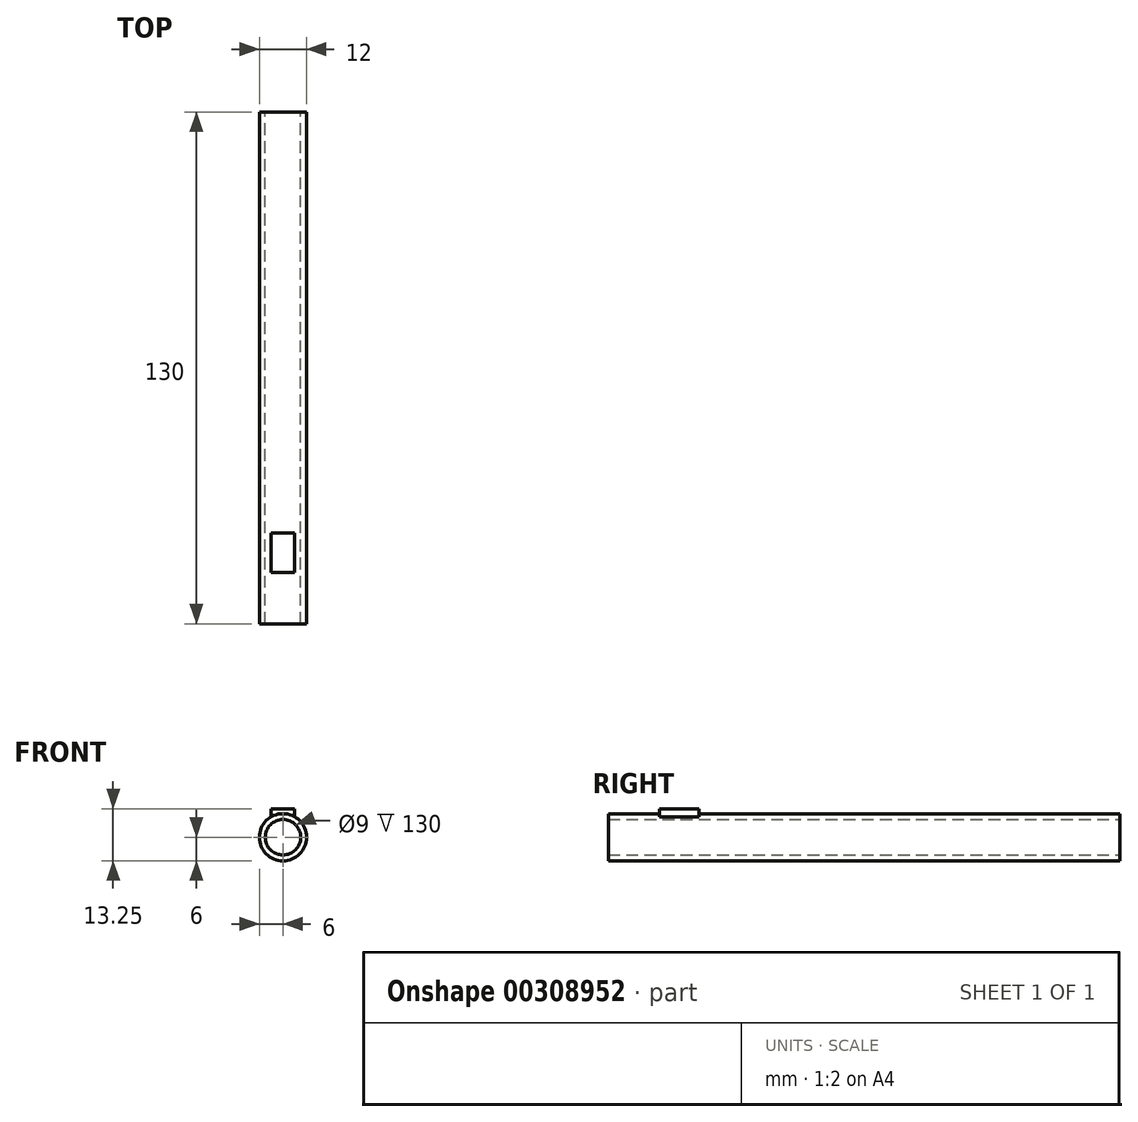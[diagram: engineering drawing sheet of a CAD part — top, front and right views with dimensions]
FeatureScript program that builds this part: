
annotation { "Feature Type Name" : "Feature", "Feature Type Description" : "" }
export const myFeature = defineFeature(function(context is Context, id is Id, definition is map)
    precondition{}
    {
        {
            var Q0;
            Q0=qCreatedBy(makeId("Front.planeOp"),FACE);
            var sketch = newSketch(context, id + "F0", { "sketchPlane" : qUnion([Q0])});
            skCircle(sketch, "E0", {"center": v(0, 0) * mm, "radius": 4.5 * mm});
            skCircle(sketch, "E1", {"center": v(0, 0) * mm, "radius": 6 * mm});
            skSolve(sketch);
        }
        {
            var Q0;
            Q0=makeQuery(id+"F0.imprint","IMPRINT",FACE,{"disambiguationData":[TD([[makeQuery(id+"F0.imprint","IMPRINT",EDGE,{"derivedFrom":sQuery(id+"F0.wireOp",EDGE,"E0")}),-1.0]])]});
            extrude(context, id + "F1", {"entities" : qUnion([Q0]), "depth" : 130 * mm, "offsetDistance" : 25 * mm});
        }
        {
            var Q0;
            Q0=makeQuery(id+"F1.opExtrude","CAP_FACE",FACE,{"disambiguationData":[OSD([sQuery(id+"F0.wireOp",EDGE,"E0"),sQuery(id+"F0.wireOp",EDGE,"E1")])],"isStart":false});
            var sketch = newSketch(context, id + "F2", { "sketchPlane" : qUnion([Q0])});
            skLineSegment(sketch, "E2.bottom", {"start": v(10, 7.25) * mm, "end": v(-10, 7.25) * mm});
            skLineSegment(sketch, "E2.top", {"start": v(10, -7.25) * mm, "end": v(-10, -7.25) * mm});
            skLineSegment(sketch, "E2.left", {"start": v(10, 7.25) * mm, "end": v(10, -7.25) * mm});
            skLineSegment(sketch, "E2.right", {"start": v(-10, 7.25) * mm, "end": v(-10, -7.25) * mm});
            skPoint(sketch, "E2.middle", {"position": v(0, 0) * mm});
            skLineSegment(sketch, "E3", {"start": v(0, 7.25) * mm, "end": v(0, 6) * mm});
            skLineSegment(sketch, "E4", {"start": v(3, 7.25) * mm, "end": v(3, 5.2) * mm});
            skLineSegment(sketch, "E5", {"start": v(-3, 7.25) * mm, "end": v(-3, 5.2) * mm});
            skSolve(sketch);
        }
        {
            var Q0;
            {var subQ0=sQuery(id+"F2.wireOp",EDGE,"E3");Q0=makeQuery(id+"F2.imprint","IMPRINT",FACE,{"disambiguationData":[TD([[makeQuery(id+"F2.imprint","IMPRINT",EDGE,{"derivedFrom":subQ0}),1.0]])]});}
            var Q1;
            {var subQ0=sQuery(id+"F2.wireOp",EDGE,"E3");Q1=makeQuery(id+"F2.imprint","IMPRINT",FACE,{"disambiguationData":[TD([[makeQuery(id+"F2.imprint","IMPRINT",EDGE,{"derivedFrom":subQ0}),-1.0]])]});}
            extrude(context, id + "F3", {"entities" : qUnion([Q0, Q1]), "operationType" : NewBodyOperationType.ADD, "oppositeDirection" : true, "depth" : 23 * mm, "offsetDistance" : 25 * mm, "hasSecondDirection" : true, "secondDirectionOppositeDirection" : false, "secondDirectionDepth" : -13 * mm});
        }
    });
